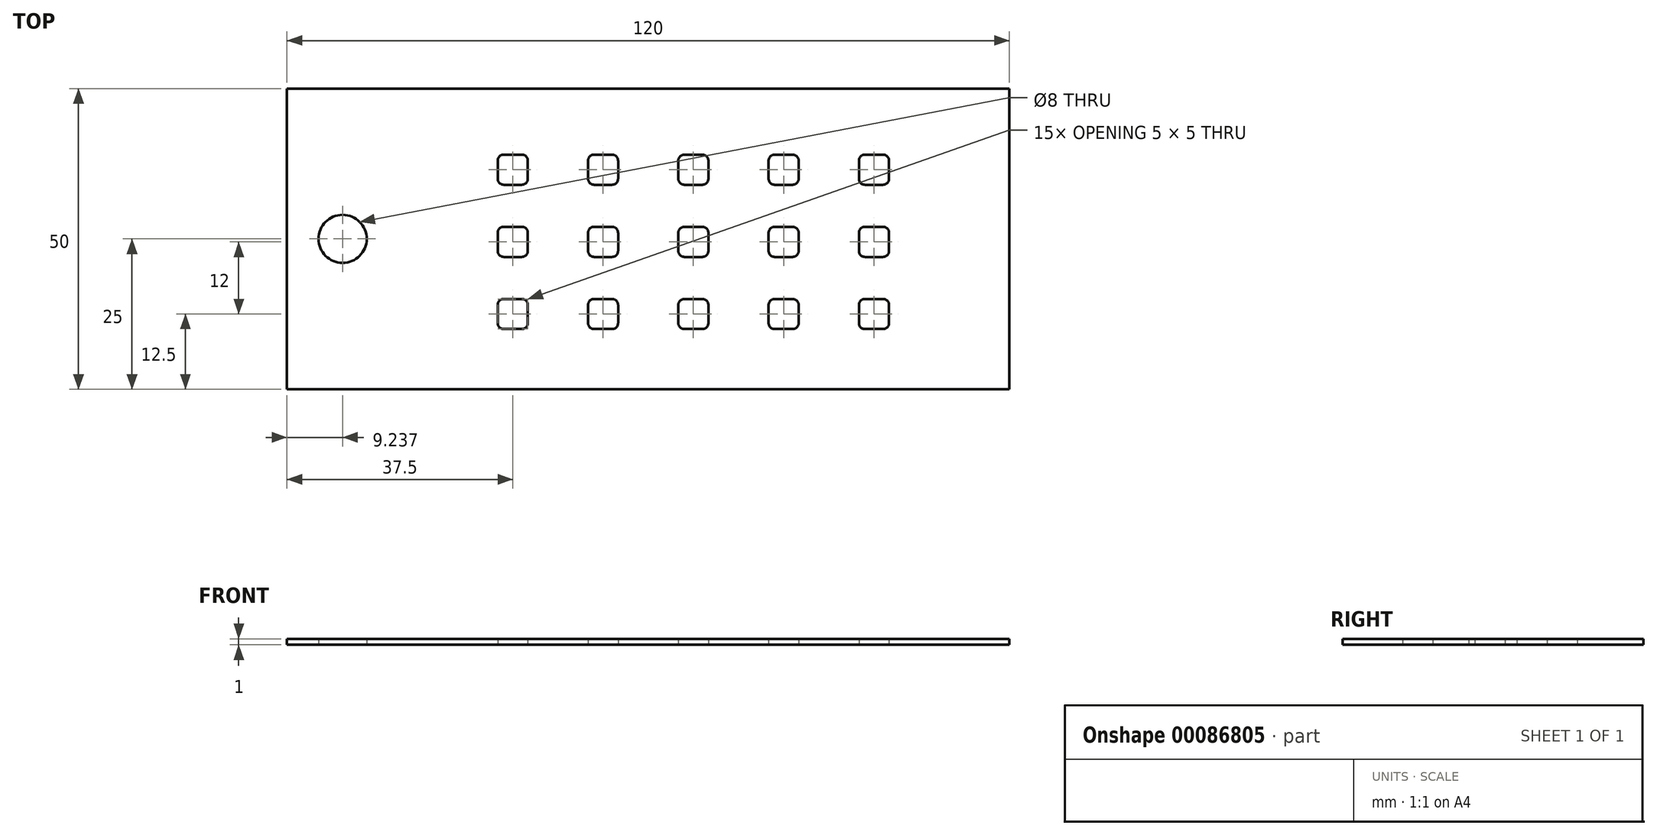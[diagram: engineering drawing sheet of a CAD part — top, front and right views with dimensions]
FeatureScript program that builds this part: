
annotation { "Feature Type Name" : "Feature", "Feature Type Description" : "" }
export const myFeature = defineFeature(function(context is Context, id is Id, definition is map)
    precondition{}
    {
        {
            var Q0;
            Q0=qCreatedBy(makeId("Top.planeOp"),FACE);
            var sketch = newSketch(context, id + "F0", { "sketchPlane" : qUnion([Q0])});
            skLineSegment(sketch, "E0.bottom", {"start": v(60, 25) * mm, "end": v(-60, 25) * mm});
            skLineSegment(sketch, "E0.top", {"start": v(60, -25) * mm, "end": v(-60, -25) * mm});
            skLineSegment(sketch, "E0.left", {"start": v(60, 25) * mm, "end": v(60, -25) * mm});
            skLineSegment(sketch, "E0.right", {"start": v(-60, 25) * mm, "end": v(-60, -25) * mm});
            skPoint(sketch, "E0.middle", {"position": v(0, 0) * mm});
            skCircle(sketch, "E1", {"center": v(-50.76, 0) * mm, "radius": 4 * mm});
            skLineSegment(sketch, "E2.bottom", {"start": v(-24, -15) * mm, "end": v(-21, -15) * mm});
            skLineSegment(sketch, "E2.top", {"start": v(-24, -10) * mm, "end": v(-21, -10) * mm});
            skLineSegment(sketch, "E2.left", {"start": v(-25, -14) * mm, "end": v(-25, -11) * mm});
            skLineSegment(sketch, "E2.right", {"start": v(-20, -14) * mm, "end": v(-20, -11) * mm});
            skPoint(sketch, "E3.visualSharp", {"position": v(-25, -10) * mm});
            skArc(sketch, "E3.filletArc", {"start": v(-24, -10) * mm, "mid": v(-24.7, -10.3) * mm, "end": v(-25, -11) * mm});
            skPoint(sketch, "E4.visualSharp", {"position": v(-20, -10) * mm});
            skArc(sketch, "E4.filletArc", {"start": v(-20, -11) * mm, "mid": v(-20.3, -10.3) * mm, "end": v(-21, -10) * mm});
            skPoint(sketch, "E5.visualSharp", {"position": v(-20, -15) * mm});
            skArc(sketch, "E5.filletArc", {"start": v(-21, -15) * mm, "mid": v(-20.3, -14.7) * mm, "end": v(-20, -14) * mm});
            skPoint(sketch, "E6.visualSharp", {"position": v(-25, -15) * mm});
            skArc(sketch, "E6.filletArc", {"start": v(-25, -14) * mm, "mid": v(-24.7, -14.7) * mm, "end": v(-24, -15) * mm});
            skPoint(sketch, "E7.0.1.0", {"position": v(-25, -3) * mm});
            skPoint(sketch, "E7.0.1.1", {"position": v(-25, 2) * mm});
            skPoint(sketch, "E7.0.1.2", {"position": v(-20, 2) * mm});
            skPoint(sketch, "E7.0.1.3", {"position": v(-20, -3) * mm});
            skLineSegment(sketch, "E7.0.1.4", {"start": v(-24, 2) * mm, "end": v(-21, 2) * mm});
            skArc(sketch, "E7.0.1.5", {"start": v(-20, 1) * mm, "mid": v(-20.3, 1.7) * mm, "end": v(-21, 2) * mm});
            skArc(sketch, "E7.0.1.6", {"start": v(-21, -3) * mm, "mid": v(-20.3, -2.7) * mm, "end": v(-20, -2) * mm});
            skLineSegment(sketch, "E7.0.1.7", {"start": v(-25, -2) * mm, "end": v(-25, 1) * mm});
            skLineSegment(sketch, "E7.0.1.8", {"start": v(-24, -3) * mm, "end": v(-21, -3) * mm});
            skLineSegment(sketch, "E7.0.1.9", {"start": v(-20, -2) * mm, "end": v(-20, 1) * mm});
            skArc(sketch, "E7.0.1.10", {"start": v(-24, 2) * mm, "mid": v(-24.7, 1.7) * mm, "end": v(-25, 1) * mm});
            skArc(sketch, "E7.0.1.11", {"start": v(-25, -2) * mm, "mid": v(-24.7, -2.7) * mm, "end": v(-24, -3) * mm});
            skPoint(sketch, "E7.0.2.0", {"position": v(-25, 9) * mm});
            skPoint(sketch, "E7.0.2.1", {"position": v(-25, 14) * mm});
            skPoint(sketch, "E7.0.2.2", {"position": v(-20, 14) * mm});
            skPoint(sketch, "E7.0.2.3", {"position": v(-20, 9) * mm});
            skLineSegment(sketch, "E7.0.2.4", {"start": v(-24, 14) * mm, "end": v(-21, 14) * mm});
            skArc(sketch, "E7.0.2.5", {"start": v(-20, 13) * mm, "mid": v(-20.3, 13.7) * mm, "end": v(-21, 14) * mm});
            skArc(sketch, "E7.0.2.6", {"start": v(-21, 9) * mm, "mid": v(-20.3, 9.3) * mm, "end": v(-20, 10) * mm});
            skLineSegment(sketch, "E7.0.2.7", {"start": v(-25, 10) * mm, "end": v(-25, 13) * mm});
            skLineSegment(sketch, "E7.0.2.8", {"start": v(-24, 9) * mm, "end": v(-21, 9) * mm});
            skLineSegment(sketch, "E7.0.2.9", {"start": v(-20, 10) * mm, "end": v(-20, 13) * mm});
            skArc(sketch, "E7.0.2.10", {"start": v(-24, 14) * mm, "mid": v(-24.7, 13.7) * mm, "end": v(-25, 13) * mm});
            skArc(sketch, "E7.0.2.11", {"start": v(-25, 10) * mm, "mid": v(-24.7, 9.3) * mm, "end": v(-24, 9) * mm});
            skPoint(sketch, "E7.1.0.0", {"position": v(-10, -15) * mm});
            skPoint(sketch, "E7.1.0.1", {"position": v(-10, -10) * mm});
            skPoint(sketch, "E7.1.0.2", {"position": v(-5, -10) * mm});
            skPoint(sketch, "E7.1.0.3", {"position": v(-5, -15) * mm});
            skLineSegment(sketch, "E7.1.0.4", {"start": v(-9, -10) * mm, "end": v(-6, -10) * mm});
            skArc(sketch, "E7.1.0.5", {"start": v(-5, -11) * mm, "mid": v(-5.3, -10.3) * mm, "end": v(-6, -10) * mm});
            skArc(sketch, "E7.1.0.6", {"start": v(-6, -15) * mm, "mid": v(-5.3, -14.7) * mm, "end": v(-5, -14) * mm});
            skLineSegment(sketch, "E7.1.0.7", {"start": v(-10, -14) * mm, "end": v(-10, -11) * mm});
            skLineSegment(sketch, "E7.1.0.8", {"start": v(-9, -15) * mm, "end": v(-6, -15) * mm});
            skLineSegment(sketch, "E7.1.0.9", {"start": v(-5, -14) * mm, "end": v(-5, -11) * mm});
            skArc(sketch, "E7.1.0.10", {"start": v(-9, -10) * mm, "mid": v(-9.7, -10.3) * mm, "end": v(-10, -11) * mm});
            skArc(sketch, "E7.1.0.11", {"start": v(-10, -14) * mm, "mid": v(-9.7, -14.7) * mm, "end": v(-9, -15) * mm});
            skPoint(sketch, "E7.1.1.0", {"position": v(-10, -3) * mm});
            skPoint(sketch, "E7.1.1.1", {"position": v(-10, 2) * mm});
            skPoint(sketch, "E7.1.1.2", {"position": v(-5, 2) * mm});
            skPoint(sketch, "E7.1.1.3", {"position": v(-5, -3) * mm});
            skLineSegment(sketch, "E7.1.1.4", {"start": v(-9, 2) * mm, "end": v(-6, 2) * mm});
            skArc(sketch, "E7.1.1.5", {"start": v(-5, 1) * mm, "mid": v(-5.3, 1.7) * mm, "end": v(-6, 2) * mm});
            skArc(sketch, "E7.1.1.6", {"start": v(-6, -3) * mm, "mid": v(-5.3, -2.7) * mm, "end": v(-5, -2) * mm});
            skLineSegment(sketch, "E7.1.1.7", {"start": v(-10, -2) * mm, "end": v(-10, 1) * mm});
            skLineSegment(sketch, "E7.1.1.8", {"start": v(-9, -3) * mm, "end": v(-6, -3) * mm});
            skLineSegment(sketch, "E7.1.1.9", {"start": v(-5, -2) * mm, "end": v(-5, 1) * mm});
            skArc(sketch, "E7.1.1.10", {"start": v(-9, 2) * mm, "mid": v(-9.7, 1.7) * mm, "end": v(-10, 1) * mm});
            skArc(sketch, "E7.1.1.11", {"start": v(-10, -2) * mm, "mid": v(-9.7, -2.7) * mm, "end": v(-9, -3) * mm});
            skPoint(sketch, "E7.1.2.0", {"position": v(-10, 9) * mm});
            skPoint(sketch, "E7.1.2.1", {"position": v(-10, 14) * mm});
            skPoint(sketch, "E7.1.2.2", {"position": v(-5, 14) * mm});
            skPoint(sketch, "E7.1.2.3", {"position": v(-5, 9) * mm});
            skLineSegment(sketch, "E7.1.2.4", {"start": v(-9, 14) * mm, "end": v(-6, 14) * mm});
            skArc(sketch, "E7.1.2.5", {"start": v(-5, 13) * mm, "mid": v(-5.3, 13.7) * mm, "end": v(-6, 14) * mm});
            skArc(sketch, "E7.1.2.6", {"start": v(-6, 9) * mm, "mid": v(-5.3, 9.3) * mm, "end": v(-5, 10) * mm});
            skLineSegment(sketch, "E7.1.2.7", {"start": v(-10, 10) * mm, "end": v(-10, 13) * mm});
            skLineSegment(sketch, "E7.1.2.8", {"start": v(-9, 9) * mm, "end": v(-6, 9) * mm});
            skLineSegment(sketch, "E7.1.2.9", {"start": v(-5, 10) * mm, "end": v(-5, 13) * mm});
            skArc(sketch, "E7.1.2.10", {"start": v(-9, 14) * mm, "mid": v(-9.7, 13.7) * mm, "end": v(-10, 13) * mm});
            skArc(sketch, "E7.1.2.11", {"start": v(-10, 10) * mm, "mid": v(-9.7, 9.3) * mm, "end": v(-9, 9) * mm});
            skPoint(sketch, "E7.2.0.0", {"position": v(5, -15) * mm});
            skPoint(sketch, "E7.2.0.1", {"position": v(5, -10) * mm});
            skPoint(sketch, "E7.2.0.2", {"position": v(10, -10) * mm});
            skPoint(sketch, "E7.2.0.3", {"position": v(10, -15) * mm});
            skLineSegment(sketch, "E7.2.0.4", {"start": v(6, -10) * mm, "end": v(9, -10) * mm});
            skArc(sketch, "E7.2.0.5", {"start": v(10, -11) * mm, "mid": v(9.7, -10.3) * mm, "end": v(9, -10) * mm});
            skArc(sketch, "E7.2.0.6", {"start": v(9, -15) * mm, "mid": v(9.7, -14.7) * mm, "end": v(10, -14) * mm});
            skLineSegment(sketch, "E7.2.0.7", {"start": v(5, -14) * mm, "end": v(5, -11) * mm});
            skLineSegment(sketch, "E7.2.0.8", {"start": v(6, -15) * mm, "end": v(9, -15) * mm});
            skLineSegment(sketch, "E7.2.0.9", {"start": v(10, -14) * mm, "end": v(10, -11) * mm});
            skArc(sketch, "E7.2.0.10", {"start": v(6, -10) * mm, "mid": v(5.3, -10.3) * mm, "end": v(5, -11) * mm});
            skArc(sketch, "E7.2.0.11", {"start": v(5, -14) * mm, "mid": v(5.3, -14.7) * mm, "end": v(6, -15) * mm});
            skPoint(sketch, "E7.2.1.0", {"position": v(5, -3) * mm});
            skPoint(sketch, "E7.2.1.1", {"position": v(5, 2) * mm});
            skPoint(sketch, "E7.2.1.2", {"position": v(10, 2) * mm});
            skPoint(sketch, "E7.2.1.3", {"position": v(10, -3) * mm});
            skLineSegment(sketch, "E7.2.1.4", {"start": v(6, 2) * mm, "end": v(9, 2) * mm});
            skArc(sketch, "E7.2.1.5", {"start": v(10, 1) * mm, "mid": v(9.7, 1.7) * mm, "end": v(9, 2) * mm});
            skArc(sketch, "E7.2.1.6", {"start": v(9, -3) * mm, "mid": v(9.7, -2.7) * mm, "end": v(10, -2) * mm});
            skLineSegment(sketch, "E7.2.1.7", {"start": v(5, -2) * mm, "end": v(5, 1) * mm});
            skLineSegment(sketch, "E7.2.1.8", {"start": v(6, -3) * mm, "end": v(9, -3) * mm});
            skLineSegment(sketch, "E7.2.1.9", {"start": v(10, -2) * mm, "end": v(10, 1) * mm});
            skArc(sketch, "E7.2.1.10", {"start": v(6, 2) * mm, "mid": v(5.3, 1.7) * mm, "end": v(5, 1) * mm});
            skArc(sketch, "E7.2.1.11", {"start": v(5, -2) * mm, "mid": v(5.3, -2.7) * mm, "end": v(6, -3) * mm});
            skPoint(sketch, "E7.2.2.0", {"position": v(5, 9) * mm});
            skPoint(sketch, "E7.2.2.1", {"position": v(5, 14) * mm});
            skPoint(sketch, "E7.2.2.2", {"position": v(10, 14) * mm});
            skPoint(sketch, "E7.2.2.3", {"position": v(10, 9) * mm});
            skLineSegment(sketch, "E7.2.2.4", {"start": v(6, 14) * mm, "end": v(9, 14) * mm});
            skArc(sketch, "E7.2.2.5", {"start": v(10, 13) * mm, "mid": v(9.7, 13.7) * mm, "end": v(9, 14) * mm});
            skArc(sketch, "E7.2.2.6", {"start": v(9, 9) * mm, "mid": v(9.7, 9.3) * mm, "end": v(10, 10) * mm});
            skLineSegment(sketch, "E7.2.2.7", {"start": v(5, 10) * mm, "end": v(5, 13) * mm});
            skLineSegment(sketch, "E7.2.2.8", {"start": v(6, 9) * mm, "end": v(9, 9) * mm});
            skLineSegment(sketch, "E7.2.2.9", {"start": v(10, 10) * mm, "end": v(10, 13) * mm});
            skArc(sketch, "E7.2.2.10", {"start": v(6, 14) * mm, "mid": v(5.3, 13.7) * mm, "end": v(5, 13) * mm});
            skArc(sketch, "E7.2.2.11", {"start": v(5, 10) * mm, "mid": v(5.3, 9.3) * mm, "end": v(6, 9) * mm});
            skPoint(sketch, "E7.3.0.0", {"position": v(20, -15) * mm});
            skPoint(sketch, "E7.3.0.1", {"position": v(20, -10) * mm});
            skPoint(sketch, "E7.3.0.2", {"position": v(25, -10) * mm});
            skPoint(sketch, "E7.3.0.3", {"position": v(25, -15) * mm});
            skLineSegment(sketch, "E7.3.0.4", {"start": v(21, -10) * mm, "end": v(24, -10) * mm});
            skArc(sketch, "E7.3.0.5", {"start": v(25, -11) * mm, "mid": v(24.7, -10.3) * mm, "end": v(24, -10) * mm});
            skArc(sketch, "E7.3.0.6", {"start": v(24, -15) * mm, "mid": v(24.7, -14.7) * mm, "end": v(25, -14) * mm});
            skLineSegment(sketch, "E7.3.0.7", {"start": v(20, -14) * mm, "end": v(20, -11) * mm});
            skLineSegment(sketch, "E7.3.0.8", {"start": v(21, -15) * mm, "end": v(24, -15) * mm});
            skLineSegment(sketch, "E7.3.0.9", {"start": v(25, -14) * mm, "end": v(25, -11) * mm});
            skArc(sketch, "E7.3.0.10", {"start": v(21, -10) * mm, "mid": v(20.3, -10.3) * mm, "end": v(20, -11) * mm});
            skArc(sketch, "E7.3.0.11", {"start": v(20, -14) * mm, "mid": v(20.3, -14.7) * mm, "end": v(21, -15) * mm});
            skPoint(sketch, "E7.3.1.0", {"position": v(20, -3) * mm});
            skPoint(sketch, "E7.3.1.1", {"position": v(20, 2) * mm});
            skPoint(sketch, "E7.3.1.2", {"position": v(25, 2) * mm});
            skPoint(sketch, "E7.3.1.3", {"position": v(25, -3) * mm});
            skLineSegment(sketch, "E7.3.1.4", {"start": v(21, 2) * mm, "end": v(24, 2) * mm});
            skArc(sketch, "E7.3.1.5", {"start": v(25, 1) * mm, "mid": v(24.7, 1.7) * mm, "end": v(24, 2) * mm});
            skArc(sketch, "E7.3.1.6", {"start": v(24, -3) * mm, "mid": v(24.7, -2.7) * mm, "end": v(25, -2) * mm});
            skLineSegment(sketch, "E7.3.1.7", {"start": v(20, -2) * mm, "end": v(20, 1) * mm});
            skLineSegment(sketch, "E7.3.1.8", {"start": v(21, -3) * mm, "end": v(24, -3) * mm});
            skLineSegment(sketch, "E7.3.1.9", {"start": v(25, -2) * mm, "end": v(25, 1) * mm});
            skArc(sketch, "E7.3.1.10", {"start": v(21, 2) * mm, "mid": v(20.3, 1.7) * mm, "end": v(20, 1) * mm});
            skArc(sketch, "E7.3.1.11", {"start": v(20, -2) * mm, "mid": v(20.3, -2.7) * mm, "end": v(21, -3) * mm});
            skPoint(sketch, "E7.3.2.0", {"position": v(20, 9) * mm});
            skPoint(sketch, "E7.3.2.1", {"position": v(20, 14) * mm});
            skPoint(sketch, "E7.3.2.2", {"position": v(25, 14) * mm});
            skPoint(sketch, "E7.3.2.3", {"position": v(25, 9) * mm});
            skLineSegment(sketch, "E7.3.2.4", {"start": v(21, 14) * mm, "end": v(24, 14) * mm});
            skArc(sketch, "E7.3.2.5", {"start": v(25, 13) * mm, "mid": v(24.7, 13.7) * mm, "end": v(24, 14) * mm});
            skArc(sketch, "E7.3.2.6", {"start": v(24, 9) * mm, "mid": v(24.7, 9.3) * mm, "end": v(25, 10) * mm});
            skLineSegment(sketch, "E7.3.2.7", {"start": v(20, 10) * mm, "end": v(20, 13) * mm});
            skLineSegment(sketch, "E7.3.2.8", {"start": v(21, 9) * mm, "end": v(24, 9) * mm});
            skLineSegment(sketch, "E7.3.2.9", {"start": v(25, 10) * mm, "end": v(25, 13) * mm});
            skArc(sketch, "E7.3.2.10", {"start": v(21, 14) * mm, "mid": v(20.3, 13.7) * mm, "end": v(20, 13) * mm});
            skArc(sketch, "E7.3.2.11", {"start": v(20, 10) * mm, "mid": v(20.3, 9.3) * mm, "end": v(21, 9) * mm});
            skPoint(sketch, "E7.4.0.0", {"position": v(35, -15) * mm});
            skPoint(sketch, "E7.4.0.1", {"position": v(35, -10) * mm});
            skPoint(sketch, "E7.4.0.2", {"position": v(40, -10) * mm});
            skPoint(sketch, "E7.4.0.3", {"position": v(40, -15) * mm});
            skLineSegment(sketch, "E7.4.0.4", {"start": v(36, -10) * mm, "end": v(39, -10) * mm});
            skArc(sketch, "E7.4.0.5", {"start": v(40, -11) * mm, "mid": v(39.7, -10.3) * mm, "end": v(39, -10) * mm});
            skArc(sketch, "E7.4.0.6", {"start": v(39, -15) * mm, "mid": v(39.7, -14.7) * mm, "end": v(40, -14) * mm});
            skLineSegment(sketch, "E7.4.0.7", {"start": v(35, -14) * mm, "end": v(35, -11) * mm});
            skLineSegment(sketch, "E7.4.0.8", {"start": v(36, -15) * mm, "end": v(39, -15) * mm});
            skLineSegment(sketch, "E7.4.0.9", {"start": v(40, -14) * mm, "end": v(40, -11) * mm});
            skArc(sketch, "E7.4.0.10", {"start": v(36, -10) * mm, "mid": v(35.3, -10.3) * mm, "end": v(35, -11) * mm});
            skArc(sketch, "E7.4.0.11", {"start": v(35, -14) * mm, "mid": v(35.3, -14.7) * mm, "end": v(36, -15) * mm});
            skPoint(sketch, "E7.4.1.0", {"position": v(35, -3) * mm});
            skPoint(sketch, "E7.4.1.1", {"position": v(35, 2) * mm});
            skPoint(sketch, "E7.4.1.2", {"position": v(40, 2) * mm});
            skPoint(sketch, "E7.4.1.3", {"position": v(40, -3) * mm});
            skLineSegment(sketch, "E7.4.1.4", {"start": v(36, 2) * mm, "end": v(39, 2) * mm});
            skArc(sketch, "E7.4.1.5", {"start": v(40, 1) * mm, "mid": v(39.7, 1.7) * mm, "end": v(39, 2) * mm});
            skArc(sketch, "E7.4.1.6", {"start": v(39, -3) * mm, "mid": v(39.7, -2.7) * mm, "end": v(40, -2) * mm});
            skLineSegment(sketch, "E7.4.1.7", {"start": v(35, -2) * mm, "end": v(35, 1) * mm});
            skLineSegment(sketch, "E7.4.1.8", {"start": v(36, -3) * mm, "end": v(39, -3) * mm});
            skLineSegment(sketch, "E7.4.1.9", {"start": v(40, -2) * mm, "end": v(40, 1) * mm});
            skArc(sketch, "E7.4.1.10", {"start": v(36, 2) * mm, "mid": v(35.3, 1.7) * mm, "end": v(35, 1) * mm});
            skArc(sketch, "E7.4.1.11", {"start": v(35, -2) * mm, "mid": v(35.3, -2.7) * mm, "end": v(36, -3) * mm});
            skPoint(sketch, "E7.4.2.0", {"position": v(35, 9) * mm});
            skPoint(sketch, "E7.4.2.1", {"position": v(35, 14) * mm});
            skPoint(sketch, "E7.4.2.2", {"position": v(40, 14) * mm});
            skPoint(sketch, "E7.4.2.3", {"position": v(40, 9) * mm});
            skLineSegment(sketch, "E7.4.2.4", {"start": v(36, 14) * mm, "end": v(39, 14) * mm});
            skArc(sketch, "E7.4.2.5", {"start": v(40, 13) * mm, "mid": v(39.7, 13.7) * mm, "end": v(39, 14) * mm});
            skArc(sketch, "E7.4.2.6", {"start": v(39, 9) * mm, "mid": v(39.7, 9.3) * mm, "end": v(40, 10) * mm});
            skLineSegment(sketch, "E7.4.2.7", {"start": v(35, 10) * mm, "end": v(35, 13) * mm});
            skLineSegment(sketch, "E7.4.2.8", {"start": v(36, 9) * mm, "end": v(39, 9) * mm});
            skLineSegment(sketch, "E7.4.2.9", {"start": v(40, 10) * mm, "end": v(40, 13) * mm});
            skArc(sketch, "E7.4.2.10", {"start": v(36, 14) * mm, "mid": v(35.3, 13.7) * mm, "end": v(35, 13) * mm});
            skArc(sketch, "E7.4.2.11", {"start": v(35, 10) * mm, "mid": v(35.3, 9.3) * mm, "end": v(36, 9) * mm});
            skLineSegment(sketch, "E7.direction1", {"start": v(-25, -15) * mm, "end": v(-10, -15) * mm, "construction": true});
            skLineSegment(sketch, "E7.direction2", {"start": v(-25, -15) * mm, "end": v(-25, -3) * mm, "construction": true});
            skSolve(sketch);
        }
        {
            var Q0;
            Q0 = qSketchRegion(id + "F0", true);
            extrude(context, id + "F1", {"entities" : qUnion([Q0]), "depth" : 1 * mm});
        }
    });
